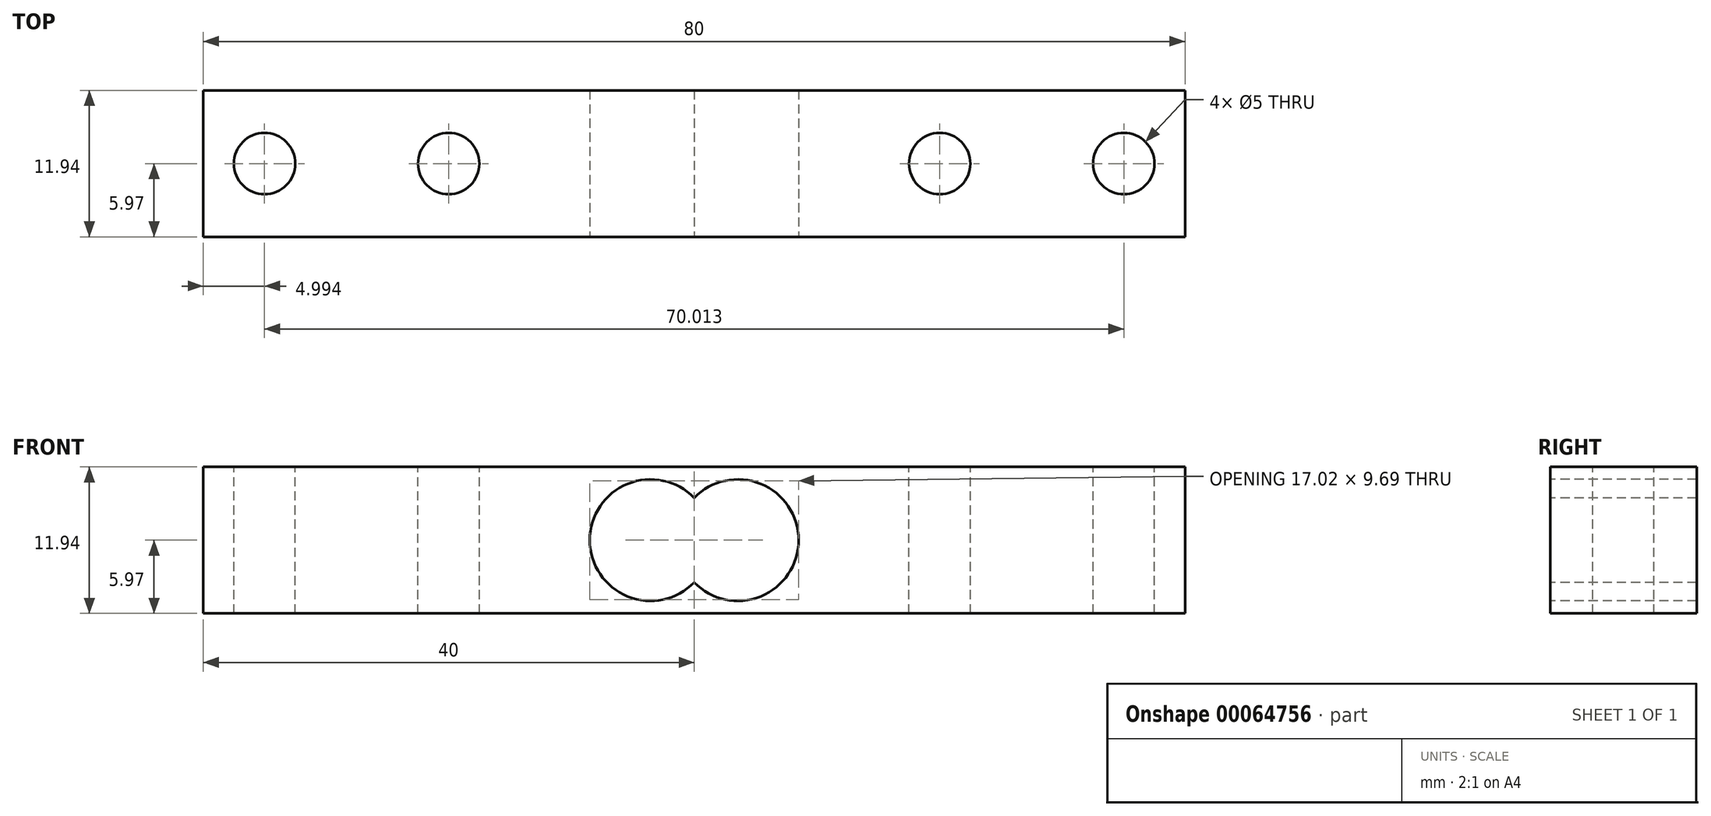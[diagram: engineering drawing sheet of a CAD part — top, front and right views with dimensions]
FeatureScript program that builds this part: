
annotation { "Feature Type Name" : "Feature", "Feature Type Description" : "" }
export const myFeature = defineFeature(function(context is Context, id is Id, definition is map)
    precondition{}
    {
        {
            var Q0;
            Q0=qCreatedBy(makeId("Right.planeOp"),FACE);
            var sketch = newSketch(context, id + "F0", { "sketchPlane" : qUnion([Q0])});
            skLineSegment(sketch, "E0.rect.bottom", {"start": v(5.97, -5.97) * mm, "end": v(-5.97, -5.97) * mm});
            skLineSegment(sketch, "E0.rect.top", {"start": v(5.97, 5.97) * mm, "end": v(-5.97, 5.97) * mm});
            skLineSegment(sketch, "E0.rect.left", {"start": v(5.97, -5.97) * mm, "end": v(5.97, 5.97) * mm});
            skLineSegment(sketch, "E0.rect.right", {"start": v(-5.97, -5.97) * mm, "end": v(-5.97, 5.97) * mm});
            skPoint(sketch, "E0.rect.middle", {"position": v(0, 0) * mm});
            skSolve(sketch);
        }
        {
            var Q0;
            Q0 = qSketchRegion(id + "F0", true);
            extrude(context, id + "F1", {"entities" : qUnion([Q0]), "endBound" : BoundingType.SYMMETRIC, "depth" : 80 * mm});
        }
        {
            var Q0;
            Q0=makeQuery(id+"F1.opExtrude","SWEPT_FACE",FACE,{"disambiguationData":[OSD([sQuery(id+"F0.wireOp",EDGE,"E0.rect.right")])]});
            var sketch = newSketch(context, id + "F2", { "sketchPlane" : qUnion([Q0])});
            skCircle(sketch, "E1", {"center": v(3.56, 0) * mm, "radius": 4.95 * mm});
            skSolve(sketch);
        }
        {
            var Q0;
            Q0 = qSketchRegion(id + "F2", true);
            extrude(context, id + "F3", {"entities" : qUnion([Q0]), "operationType" : NewBodyOperationType.REMOVE, "oppositeDirection" : true, "depth" : 25.4 * mm});
        }
        {
            var Q0;
            Q0=makeQuery(id+"F1.opExtrude","SWEPT_FACE",FACE,{"disambiguationData":[OSD([sQuery(id+"F0.wireOp",EDGE,"E0.rect.right")])]});
            var sketch = newSketch(context, id + "F4", { "sketchPlane" : qUnion([Q0])});
            skCircle(sketch, "E2", {"center": v(-3.56, 0) * mm, "radius": 4.95 * mm});
            skSolve(sketch);
        }
        {
            var Q0;
            Q0 = qSketchRegion(id + "F4", true);
            extrude(context, id + "F5", {"entities" : qUnion([Q0]), "operationType" : NewBodyOperationType.REMOVE, "endBound" : BoundingType.THROUGH_ALL, "oppositeDirection" : true, "depth" : 25.4 * mm});
        }
        {
            var Q0;
            Q0=makeQuery(id+"F1.opExtrude","SWEPT_FACE",FACE,{"disambiguationData":[OSD([sQuery(id+"F0.wireOp",EDGE,"E0.rect.top")])]});
            var sketch = newSketch(context, id + "F6", { "sketchPlane" : qUnion([Q0])});
            skCircle(sketch, "E3", {"center": v(-35, 0) * mm, "radius": 2.5 * mm});
            skCircle(sketch, "E4", {"center": v(-20, 0) * mm, "radius": 2.5 * mm});
            skCircle(sketch, "E5.MirrorC", {"center": v(20, 0) * mm, "radius": 2.5 * mm});
            skCircle(sketch, "E6.MirrorC", {"center": v(35, 0) * mm, "radius": 2.5 * mm});
            skSolve(sketch);
        }
        {
            var Q0;
            Q0 = qSketchRegion(id + "F6", true);
            extrude(context, id + "F7", {"entities" : qUnion([Q0]), "operationType" : NewBodyOperationType.REMOVE, "endBound" : BoundingType.THROUGH_ALL, "oppositeDirection" : true, "depth" : 25.4 * mm});
        }
    });
